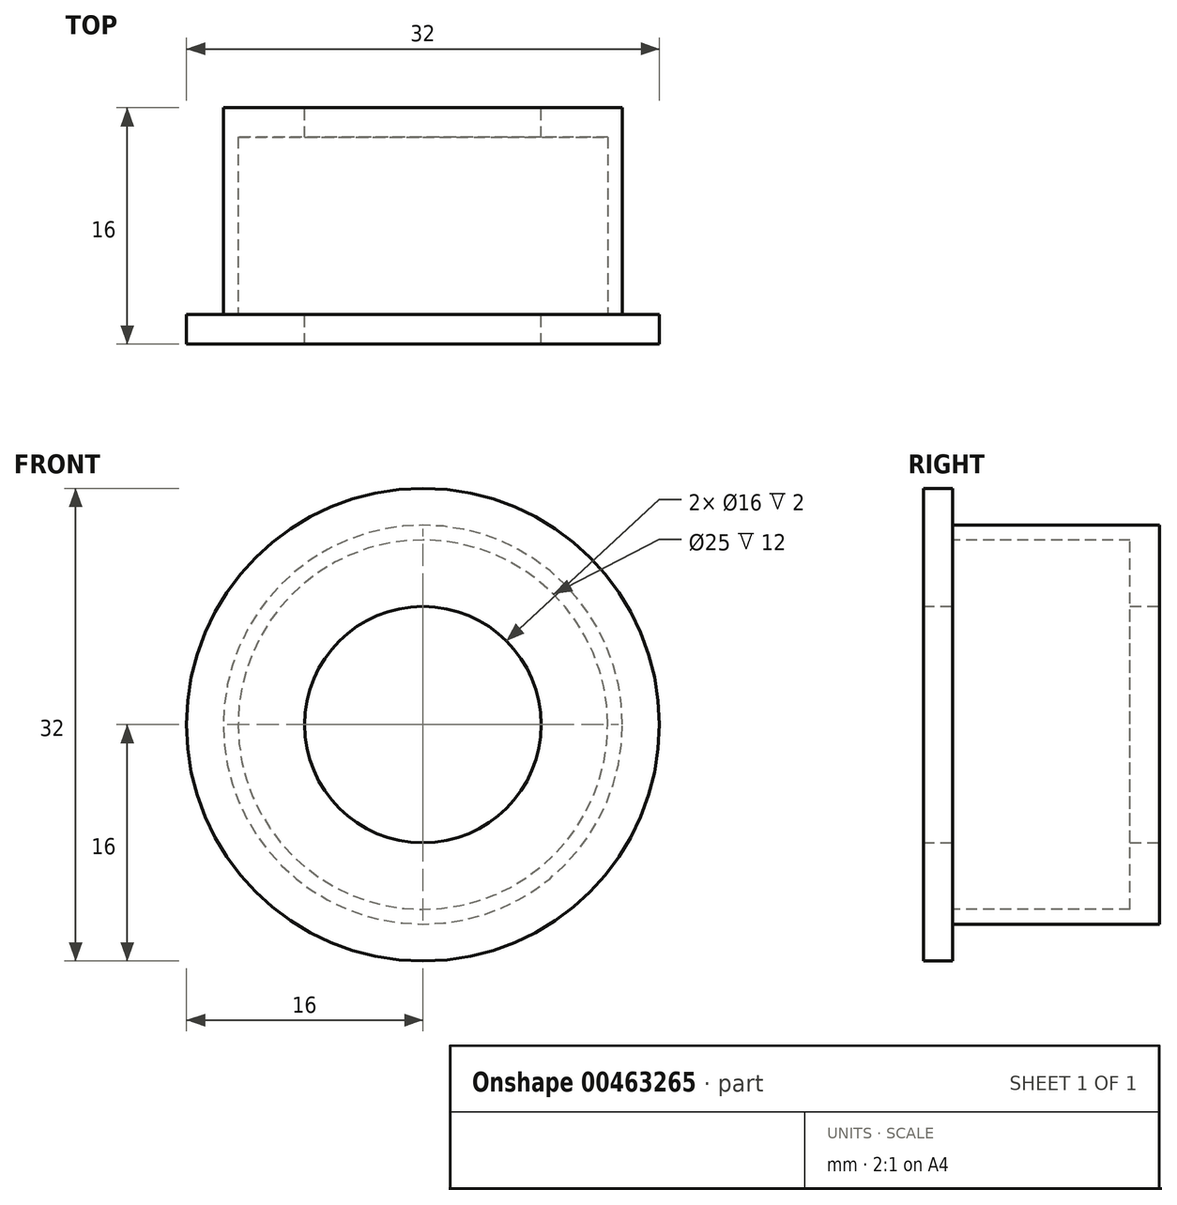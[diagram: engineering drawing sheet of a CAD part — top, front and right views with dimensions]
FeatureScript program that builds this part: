
annotation { "Feature Type Name" : "Feature", "Feature Type Description" : "" }
export const myFeature = defineFeature(function(context is Context, id is Id, definition is map)
    precondition{}
    {
        {
            var Q0;
            Q0=qCreatedBy(makeId("Front.planeOp"),FACE);
            var sketch = newSketch(context, id + "F0", { "sketchPlane" : qUnion([Q0])});
            skCircle(sketch, "E0", {"center": v(0, 0) * mm, "radius": 13.5 * mm});
            skCircle(sketch, "E1", {"center": v(0, 0) * mm, "radius": 8 * mm});
            skSolve(sketch);
        }
        {
            var Q0;
            Q0 = qSketchRegion(id + "F0", true);
            extrude(context, id + "F1", {"entities" : qUnion([Q0]), "depth" : 14 * mm});
        }
        {
            var Q0;
            Q0=makeQuery(id+"F1.opExtrude","CAP_FACE",FACE,{"disambiguationData":[OSD([sQuery(id+"F0.wireOp",EDGE,"E0"),sQuery(id+"F0.wireOp",EDGE,"E1")])],"isStart":false});
            var sketch = newSketch(context, id + "F2", { "sketchPlane" : qUnion([Q0])});
            skCircle(sketch, "E2", {"center": v(0, 0) * mm, "radius": 12.5 * mm});
            skSolve(sketch);
        }
        {
            var Q0;
            Q0 = qSketchRegion(id + "F2", true);
            extrude(context, id + "F3", {"entities" : qUnion([Q0]), "operationType" : NewBodyOperationType.REMOVE, "oppositeDirection" : true, "depth" : 12 * mm});
        }
        {
            var Q0;
            Q0=makeQuery(id+"F1.opExtrude","CAP_FACE",FACE,{"disambiguationData":[OSD([sQuery(id+"F0.wireOp",EDGE,"E0"),sQuery(id+"F0.wireOp",EDGE,"E1")])],"isStart":false});
            var sketch = newSketch(context, id + "F4", { "sketchPlane" : qUnion([Q0])});
            skCircle(sketch, "E3", {"center": v(0, 0) * mm, "radius": 16 * mm});
            skCircle(sketch, "E4", {"center": v(0, 0) * mm, "radius": 8 * mm});
            skSolve(sketch);
        }
        {
            var Q0;
            Q0 = qSketchRegion(id + "F4", true);
            extrude(context, id + "F5", {"entities" : qUnion([Q0]), "operationType" : NewBodyOperationType.ADD, "depth" : 2 * mm});
        }
    });
